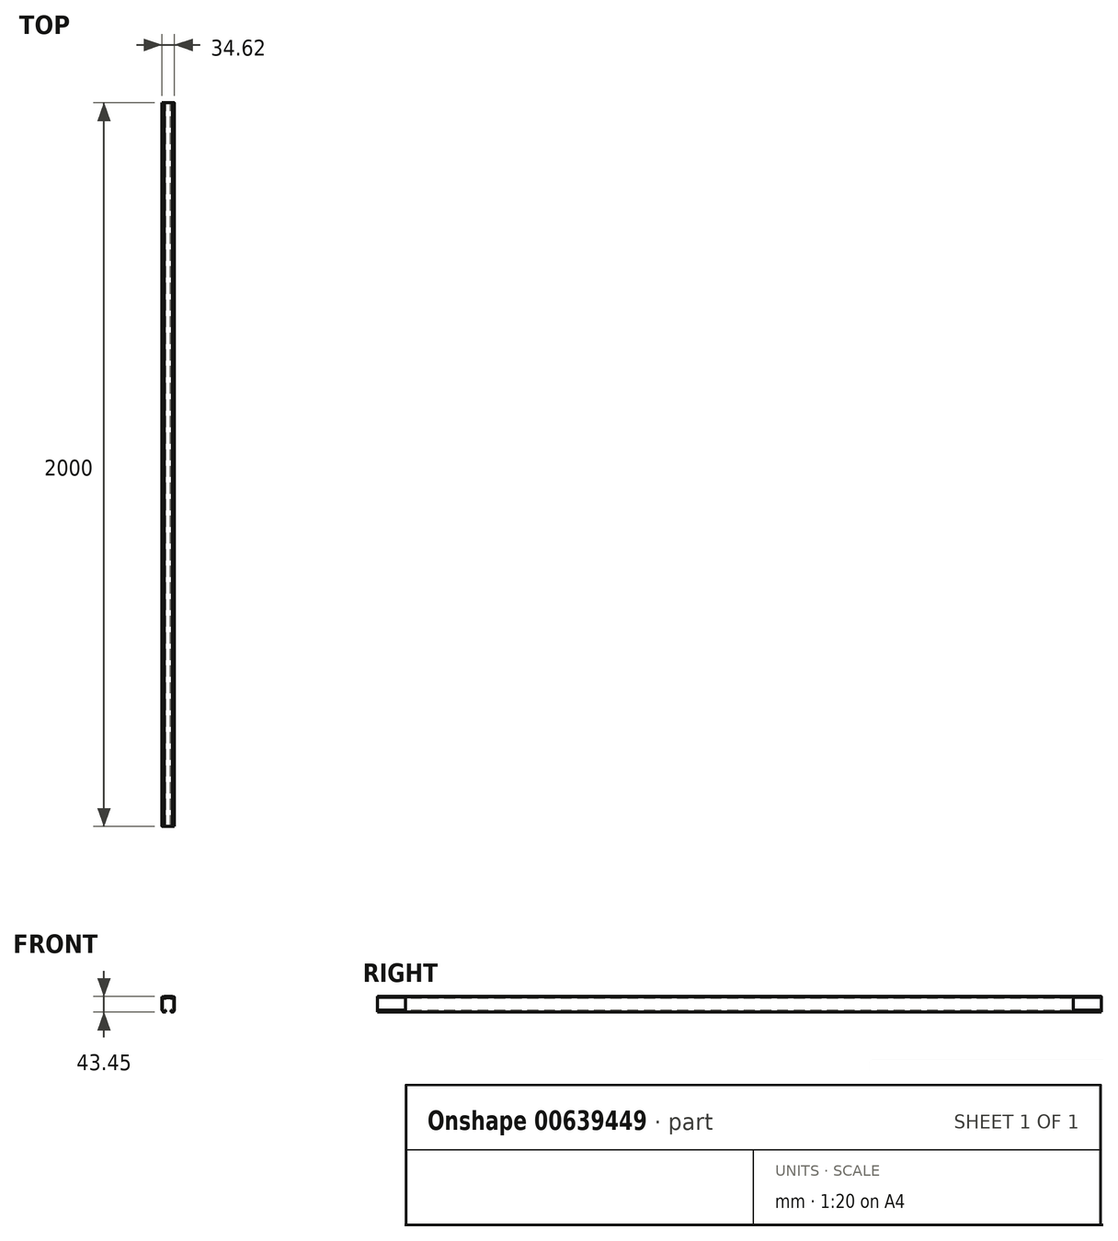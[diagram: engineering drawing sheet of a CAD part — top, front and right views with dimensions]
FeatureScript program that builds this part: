
annotation { "Feature Type Name" : "Feature", "Feature Type Description" : "" }
export const myFeature = defineFeature(function(context is Context, id is Id, definition is map)
    precondition{}
    {
        {
            var Q0;
            Q0=qCreatedBy(makeId("Front.planeOp"),FACE);
            var sketch = newSketch(context, id + "F0", { "sketchPlane" : qUnion([Q0])});
            skLineSegment(sketch, "E0", {"start": v(0, 42.5) * mm, "end": v(-10.7, 42.5) * mm});
            skLineSegment(sketch, "E1", {"start": v(-11.2, 42) * mm, "end": v(-11.2, 41.8) * mm});
            skLineSegment(sketch, "E2", {"start": v(-11.7, 41.3) * mm, "end": v(-16.8, 41.3) * mm});
            skPoint(sketch, "E3.visualSharp", {"position": v(-17.3, 41.3) * mm});
            skArc(sketch, "E3.filletArc", {"start": v(-16.8, 41.3) * mm, "mid": v(-17.15, 41.15) * mm, "end": v(-17.3, 40.8) * mm});
            skPoint(sketch, "E4.visualSharp", {"position": v(-11.2, 41.3) * mm});
            skArc(sketch, "E4.filletArc", {"start": v(-11.7, 41.3) * mm, "mid": v(-11.35, 41.45) * mm, "end": v(-11.2, 41.8) * mm});
            skPoint(sketch, "E5.visualSharp", {"position": v(-11.2, 42.5) * mm});
            skArc(sketch, "E5.filletArc", {"start": v(-10.7, 42.5) * mm, "mid": v(-11.05, 42.35) * mm, "end": v(-11.2, 42) * mm});
            skLineSegment(sketch, "E6", {"start": v(0, 39.5) * mm, "end": v(-6.5, 39.5) * mm});
            skLineSegment(sketch, "E7", {"start": v(-7, 39) * mm, "end": v(-7, 38) * mm});
            skLineSegment(sketch, "E8", {"start": v(-17.3, 41.3) * mm, "end": v(-17.3, 4.44) * mm});
            skLineSegment(sketch, "E9", {"start": v(-7.93, 0.05) * mm, "end": v(-7.93, 4.05) * mm});
            skLineSegment(sketch, "E10", {"start": v(-8.43, 4.55) * mm, "end": v(-8.43, 4.55) * mm});
            skLineSegment(sketch, "E11", {"start": v(-8.93, 4.05) * mm, "end": v(-8.93, 1.05) * mm});
            skLineSegment(sketch, "E12", {"start": v(-9.43, 0.55) * mm, "end": v(-13.58, 0.55) * mm});
            skLineSegment(sketch, "E13", {"start": v(-14.08, 1.05) * mm, "end": v(-14.08, 4.05) * mm});
            skLineSegment(sketch, "E14", {"start": v(-14.58, 4.55) * mm, "end": v(-15.42, 4.55) * mm});
            skPoint(sketch, "E15.visualSharp", {"position": v(-7.93, -0.95) * mm});
            skArc(sketch, "E15.filletArc", {"start": v(-8.93, -0.95) * mm, "mid": v(-8.22, -0.66) * mm, "end": v(-7.93, 0.05) * mm});
            skLineSegment(sketch, "E16", {"start": v(-8.93, -0.95) * mm, "end": v(-13.91, -0.95) * mm});
            skLineSegment(sketch, "E17", {"start": v(-14.34, -0.7) * mm, "end": v(-17.23, 4.18) * mm});
            skPoint(sketch, "E18.visualSharp", {"position": v(-14.2, -0.95) * mm});
            skArc(sketch, "E18.filletArc", {"start": v(-14.34, -0.7) * mm, "mid": v(-14.16, -0.88) * mm, "end": v(-13.91, -0.95) * mm});
            skPoint(sketch, "E19.visualSharp", {"position": v(-14.08, 0.55) * mm});
            skArc(sketch, "E19.filletArc", {"start": v(-14.08, 1.05) * mm, "mid": v(-13.93, 0.7) * mm, "end": v(-13.58, 0.55) * mm});
            skPoint(sketch, "E20.visualSharp", {"position": v(-8.93, 0.55) * mm});
            skArc(sketch, "E20.filletArc", {"start": v(-9.43, 0.55) * mm, "mid": v(-9.08, 0.7) * mm, "end": v(-8.93, 1.05) * mm});
            skPoint(sketch, "E21.visualSharp", {"position": v(-8.93, 4.55) * mm});
            skArc(sketch, "E21.filletArc", {"start": v(-8.43, 4.55) * mm, "mid": v(-8.78, 4.4) * mm, "end": v(-8.93, 4.05) * mm});
            skPoint(sketch, "E22.visualSharp", {"position": v(-7.93, 4.55) * mm});
            skArc(sketch, "E22.filletArc", {"start": v(-7.93, 4.05) * mm, "mid": v(-8.08, 4.4) * mm, "end": v(-8.43, 4.55) * mm});
            skPoint(sketch, "E23.visualSharp", {"position": v(-14.08, 4.55) * mm});
            skArc(sketch, "E23.filletArc", {"start": v(-14.08, 4.05) * mm, "mid": v(-14.23, 4.4) * mm, "end": v(-14.58, 4.55) * mm});
            skPoint(sketch, "E24.visualSharp", {"position": v(-15.93, 4.55) * mm});
            skArc(sketch, "E24.filletArc", {"start": v(-15.92, 5.06) * mm, "mid": v(-15.78, 4.7) * mm, "end": v(-15.42, 4.55) * mm});
            skPoint(sketch, "E25.visualSharp", {"position": v(-17.3, 4.3) * mm});
            skArc(sketch, "E25.filletArc", {"start": v(-17.3, 4.44) * mm, "mid": v(-17.28, 4.3) * mm, "end": v(-17.23, 4.18) * mm});
            skPoint(sketch, "E26.visualSharp", {"position": v(-7, 37.5) * mm});
            skArc(sketch, "E26.filletArc", {"start": v(-7.5, 37.5) * mm, "mid": v(-7.15, 37.65) * mm, "end": v(-7, 38) * mm});
            skPoint(sketch, "E27.visualSharp", {"position": v(-7, 39.5) * mm});
            skArc(sketch, "E27.filletArc", {"start": v(-6.5, 39.5) * mm, "mid": v(-6.85, 39.35) * mm, "end": v(-7, 39) * mm});
            skArc(sketch, "E28.MirrorCS", {"start": v(14.08, 4.05) * mm, "mid": v(14.23, 4.4) * mm, "end": v(14.58, 4.55) * mm});
            skArc(sketch, "E29.MirrorCS", {"start": v(7.93, 4.05) * mm, "mid": v(8.08, 4.4) * mm, "end": v(8.43, 4.55) * mm});
            skLineSegment(sketch, "E30.MirrorCS", {"start": v(14.58, 4.55) * mm, "end": v(15.42, 4.55) * mm});
            skLineSegment(sketch, "E31.MirrorCS", {"start": v(7, 39) * mm, "end": v(7, 38) * mm});
            skArc(sketch, "E32.MirrorCS", {"start": v(9.43, 0.55) * mm, "mid": v(9.08, 0.7) * mm, "end": v(8.93, 1.05) * mm});
            skArc(sketch, "E33.MirrorCS", {"start": v(15.92, 5.06) * mm, "mid": v(15.78, 4.7) * mm, "end": v(15.42, 4.55) * mm});
            skArc(sketch, "E34.MirrorCS", {"start": v(6.5, 39.5) * mm, "mid": v(6.85, 39.35) * mm, "end": v(7, 39) * mm});
            skArc(sketch, "E35.MirrorCS", {"start": v(8.43, 4.55) * mm, "mid": v(8.78, 4.4) * mm, "end": v(8.93, 4.05) * mm});
            skLineSegment(sketch, "E36.MirrorCS", {"start": v(11.2, 42) * mm, "end": v(11.2, 41.8) * mm});
            skArc(sketch, "E37.MirrorCS", {"start": v(14.08, 1.05) * mm, "mid": v(13.93, 0.7) * mm, "end": v(13.58, 0.55) * mm});
            skArc(sketch, "E38.MirrorCS", {"start": v(17.3, 4.44) * mm, "mid": v(17.28, 4.3) * mm, "end": v(17.23, 4.18) * mm});
            skArc(sketch, "E39.MirrorCS", {"start": v(10.7, 42.5) * mm, "mid": v(11.05, 42.35) * mm, "end": v(11.2, 42) * mm});
            skArc(sketch, "E40.MirrorCS", {"start": v(7.5, 37.5) * mm, "mid": v(7.15, 37.65) * mm, "end": v(7, 38) * mm});
            skArc(sketch, "E41.MirrorCS", {"start": v(11.7, 41.3) * mm, "mid": v(11.35, 41.45) * mm, "end": v(11.2, 41.8) * mm});
            skArc(sketch, "E42.MirrorCS", {"start": v(14.34, -0.7) * mm, "mid": v(14.16, -0.88) * mm, "end": v(13.91, -0.95) * mm});
            skArc(sketch, "E43.MirrorCS", {"start": v(8.93, -0.95) * mm, "mid": v(8.22, -0.66) * mm, "end": v(7.93, 0.05) * mm});
            skArc(sketch, "E44.MirrorCS", {"start": v(16.8, 41.3) * mm, "mid": v(17.15, 41.15) * mm, "end": v(17.3, 40.8) * mm});
            skLineSegment(sketch, "E45.MirrorCS", {"start": v(9.43, 0.55) * mm, "end": v(13.58, 0.55) * mm});
            skPoint(sketch, "E46.MirrorP", {"position": v(8.93, 0.55) * mm});
            skLineSegment(sketch, "E47.MirrorCS", {"start": v(7.93, 0.05) * mm, "end": v(7.93, 4.05) * mm});
            skLineSegment(sketch, "E48.MirrorCS", {"start": v(8.93, -0.95) * mm, "end": v(13.91, -0.95) * mm});
            skPoint(sketch, "E49.MirrorP", {"position": v(7, 37.5) * mm});
            skPoint(sketch, "E50.MirrorP", {"position": v(14.08, 0.55) * mm});
            skPoint(sketch, "E51.MirrorP", {"position": v(7.93, -0.95) * mm});
            skLineSegment(sketch, "E52.MirrorCS", {"start": v(0, 42.5) * mm, "end": v(10.7, 42.5) * mm});
            skLineSegment(sketch, "E53.MirrorCS", {"start": v(14.08, 1.05) * mm, "end": v(14.08, 4.05) * mm});
            skLineSegment(sketch, "E54.MirrorCS", {"start": v(17.3, 41.3) * mm, "end": v(17.3, 4.44) * mm});
            skPoint(sketch, "E55.MirrorP", {"position": v(7, 39.5) * mm});
            skPoint(sketch, "E56.MirrorP", {"position": v(15.93, 4.55) * mm});
            skPoint(sketch, "E57.MirrorP", {"position": v(7.93, 4.55) * mm});
            skLineSegment(sketch, "E58.MirrorCS", {"start": v(0, 39.5) * mm, "end": v(6.5, 39.5) * mm});
            skPoint(sketch, "E59.MirrorP", {"position": v(14.2, -0.95) * mm});
            skPoint(sketch, "E60.MirrorP", {"position": v(11.2, 42.5) * mm});
            skLineSegment(sketch, "E61.MirrorCS", {"start": v(14.34, -0.7) * mm, "end": v(17.23, 4.18) * mm});
            skPoint(sketch, "E62.MirrorP", {"position": v(17.3, 41.3) * mm});
            skPoint(sketch, "E63.MirrorP", {"position": v(17.3, 4.3) * mm});
            skPoint(sketch, "E64.MirrorP", {"position": v(11.2, 41.3) * mm});
            skLineSegment(sketch, "E65.MirrorCS", {"start": v(8.93, 4.05) * mm, "end": v(8.93, 1.05) * mm});
            skLineSegment(sketch, "E66.MirrorCS", {"start": v(8.43, 4.55) * mm, "end": v(8.43, 4.55) * mm});
            skPoint(sketch, "E67.MirrorP", {"position": v(8.93, 4.55) * mm});
            skLineSegment(sketch, "E68.MirrorCS", {"start": v(11.7, 41.3) * mm, "end": v(16.8, 41.3) * mm});
            skPoint(sketch, "E69.MirrorP", {"position": v(14.08, 4.55) * mm});
            skLineSegment(sketch, "E70", {"start": v(7.5, 37.5) * mm, "end": v(10.93, 37.5) * mm});
            skLineSegment(sketch, "E71", {"start": v(15.92, 5.06) * mm, "end": v(15.92, 32.5) * mm});
            skLineSegment(sketch, "E72", {"start": v(-15.92, 5.06) * mm, "end": v(-15.92, 32.5) * mm});
            skLineSegment(sketch, "E73", {"start": v(-7.5, 37.5) * mm, "end": v(-10.93, 37.5) * mm});
            skPoint(sketch, "E74.visualSharp", {"position": v(-15.92, 37.5) * mm});
            skArc(sketch, "E74.filletArc", {"start": v(-10.93, 37.5) * mm, "mid": v(-14.46, 36.03) * mm, "end": v(-15.92, 32.5) * mm});
            skPoint(sketch, "E75.visualSharp", {"position": v(15.92, 37.5) * mm});
            skArc(sketch, "E75.filletArc", {"start": v(15.92, 32.5) * mm, "mid": v(14.46, 36.03) * mm, "end": v(10.93, 37.5) * mm});
            skSolve(sketch);
        }
        {
            var Q0;
            Q0=makeQuery(id+"F0.imprint","IMPRINT",FACE,{"disambiguationData":[TD([[makeQuery(id+"F0.imprint","IMPRINT",EDGE,{"derivedFrom":sQuery(id+"F0.wireOp",EDGE,"E0")}),1.0]])]});
            extrude(context, id + "F1", {"entities" : qUnion([Q0]), "depth" : 2000 * mm, "offsetDistance" : 25 * mm});
        }
        {
            var Q0;
            Q0=makeQuery(id+"F1.opExtrude","SWEPT_FACE",FACE,{"disambiguationData":[OSD([sQuery(id+"F0.wireOp",EDGE,"E54.MirrorCS")])]});
            var sketch = newSketch(context, id + "F2", { "sketchPlane" : qUnion([Q0])});
            skLineSegment(sketch, "E76.bottom", {"start": v(-2000, 40.8) * mm, "end": v(-1922.55, 40.8) * mm});
            skLineSegment(sketch, "E76.top", {"start": v(-2000, 4.44) * mm, "end": v(-1922.55, 4.44) * mm});
            skLineSegment(sketch, "E76.left", {"start": v(-2000, 40.8) * mm, "end": v(-2000, 4.44) * mm});
            skLineSegment(sketch, "E76.right", {"start": v(-1922.55, 40.8) * mm, "end": v(-1922.55, 4.44) * mm});
            skSolve(sketch);
        }
        {
            var Q0;
            Q0 = qSketchRegion(id + "F2", true);
            extrude(context, id + "F3", {"entities" : qUnion([Q0]), "operationType" : NewBodyOperationType.ADD, "depth" : 0.01 * mm, "offsetDistance" : 25 * mm});
        }
        {
            var Q0;
            Q0=makeQuery(id+"F1.opExtrude","SWEPT_FACE",FACE,{"disambiguationData":[OSD([sQuery(id+"F0.wireOp",EDGE,"E8")])]});
            var sketch = newSketch(context, id + "F4", { "sketchPlane" : qUnion([Q0])});
            skLineSegment(sketch, "E77.bottom", {"start": v(2000, 40.8) * mm, "end": v(1922.37, 40.8) * mm});
            skLineSegment(sketch, "E77.top", {"start": v(2000, 4.44) * mm, "end": v(1922.37, 4.44) * mm});
            skLineSegment(sketch, "E77.left", {"start": v(2000, 40.8) * mm, "end": v(2000, 4.44) * mm});
            skLineSegment(sketch, "E77.right", {"start": v(1922.37, 40.8) * mm, "end": v(1922.37, 4.44) * mm});
            skSolve(sketch);
        }
        {
            var Q0;
            Q0 = qSketchRegion(id + "F4", true);
            extrude(context, id + "F5", {"entities" : qUnion([Q0]), "operationType" : NewBodyOperationType.ADD, "depth" : 0.01 * mm, "offsetDistance" : 25 * mm});
        }
        {
            var Q0;
            Q0=makeQuery(id+"F1.opExtrude","SWEPT_FACE",FACE,{"disambiguationData":[OSD([sQuery(id+"F0.wireOp",EDGE,"E8")])]});
            var sketch = newSketch(context, id + "F6", { "sketchPlane" : qUnion([Q0])});
            skLineSegment(sketch, "E78.bottom", {"start": v(0, 40.8) * mm, "end": v(77.45, 40.8) * mm});
            skLineSegment(sketch, "E78.top", {"start": v(0, 4.44) * mm, "end": v(77.45, 4.44) * mm});
            skLineSegment(sketch, "E78.left", {"start": v(0, 40.8) * mm, "end": v(0, 4.44) * mm});
            skLineSegment(sketch, "E78.right", {"start": v(77.45, 40.8) * mm, "end": v(77.45, 4.44) * mm});
            skSolve(sketch);
        }
        {
            var Q0;
            Q0 = qSketchRegion(id + "F6", true);
            extrude(context, id + "F7", {"entities" : qUnion([Q0]), "operationType" : NewBodyOperationType.ADD, "depth" : 0.01 * mm, "offsetDistance" : 25 * mm});
        }
        {
            var Q0;
            Q0=makeQuery(id+"F1.opExtrude","SWEPT_FACE",FACE,{"disambiguationData":[OSD([sQuery(id+"F0.wireOp",EDGE,"E54.MirrorCS")])]});
            var sketch = newSketch(context, id + "F8", { "sketchPlane" : qUnion([Q0])});
            skLineSegment(sketch, "E79.bottom", {"start": v(0, 40.8) * mm, "end": v(-77.3, 40.8) * mm});
            skLineSegment(sketch, "E79.top", {"start": v(0, 4.44) * mm, "end": v(-77.3, 4.44) * mm});
            skLineSegment(sketch, "E79.left", {"start": v(0, 40.8) * mm, "end": v(0, 4.44) * mm});
            skLineSegment(sketch, "E79.right", {"start": v(-77.3, 40.8) * mm, "end": v(-77.3, 4.44) * mm});
            skSolve(sketch);
        }
        {
            var Q0;
            Q0 = qSketchRegion(id + "F8", true);
            extrude(context, id + "F9", {"entities" : qUnion([Q0]), "operationType" : NewBodyOperationType.ADD, "depth" : 0.01 * mm, "offsetDistance" : 25 * mm});
        }
    });
